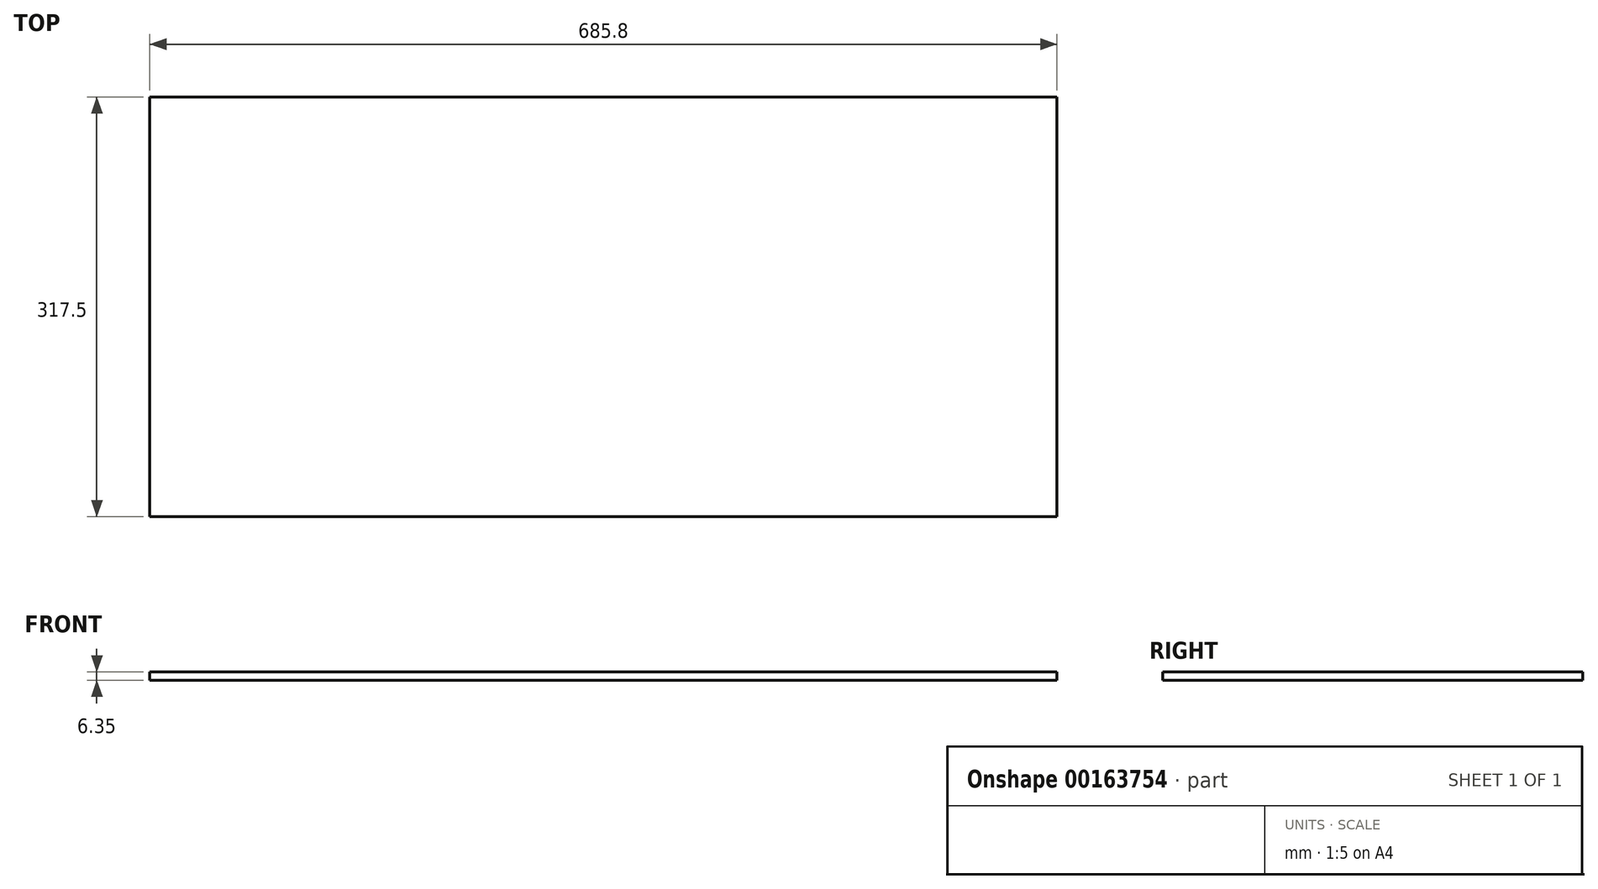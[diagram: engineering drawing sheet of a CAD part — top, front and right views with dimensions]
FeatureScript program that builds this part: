
annotation { "Feature Type Name" : "Feature", "Feature Type Description" : "" }
export const myFeature = defineFeature(function(context is Context, id is Id, definition is map)
    precondition{}
    {
        {
            var Q0;
            Q0=qCreatedBy(makeId("Top.planeOp"),FACE);
            var sketch = newSketch(context, id + "F0", { "sketchPlane" : qUnion([Q0])});
            skLineSegment(sketch, "E0.bottom", {"start": v(342.9, 158.75) * mm, "end": v(-342.9, 158.75) * mm});
            skLineSegment(sketch, "E0.top", {"start": v(342.9, -158.75) * mm, "end": v(-342.9, -158.75) * mm});
            skLineSegment(sketch, "E0.left", {"start": v(342.9, 158.75) * mm, "end": v(342.9, -158.75) * mm});
            skLineSegment(sketch, "E0.right", {"start": v(-342.9, 158.75) * mm, "end": v(-342.9, -158.75) * mm});
            skPoint(sketch, "E0.middle", {"position": v(0, 0) * mm});
            skSolve(sketch);
        }
        {
            var Q0;
            Q0=qSketchRegion(id+"F0",true);
            extrude(context, id + "F1", {"entities" : qUnion([Q0]), "depth" : 6.35 * mm, "offsetDistance" : 25.4 * mm});
        }
    });
